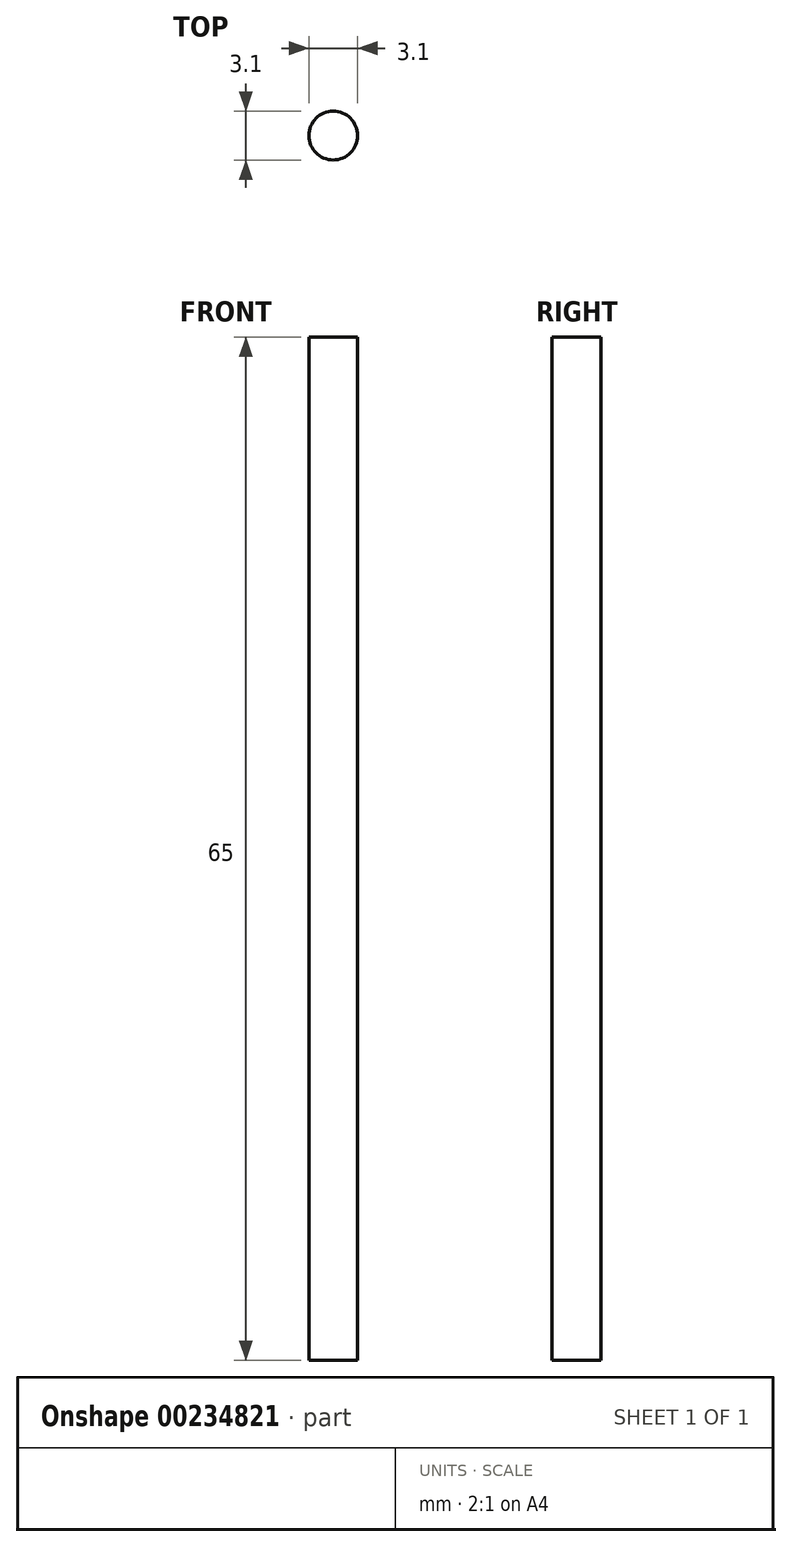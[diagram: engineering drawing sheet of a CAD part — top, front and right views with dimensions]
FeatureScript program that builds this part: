
annotation { "Feature Type Name" : "Feature", "Feature Type Description" : "" }
export const myFeature = defineFeature(function(context is Context, id is Id, definition is map)
    precondition{}
    {
        {
            var Q0;
            Q0=qCreatedBy(makeId("Top.planeOp"),FACE);
            var sketch = newSketch(context, id + "F0", { "sketchPlane" : qUnion([Q0])});
            skCircle(sketch, "E0", {"center": v(0, 0) * mm, "radius": 1.55 * mm});
            skSolve(sketch);
        }
        {
            var Q0;
            Q0=makeQuery(id+"F0.imprint","IMPRINT",FACE,{"disambiguationData":[TD([[makeQuery(id+"F0.imprint","IMPRINT",EDGE,{"derivedFrom":sQuery(id+"F0.wireOp",EDGE,"E0")}),1.0]])]});
            extrude(context, id + "F1", {"entities" : qUnion([Q0]), "depth" : 65 * mm});
        }
    });
